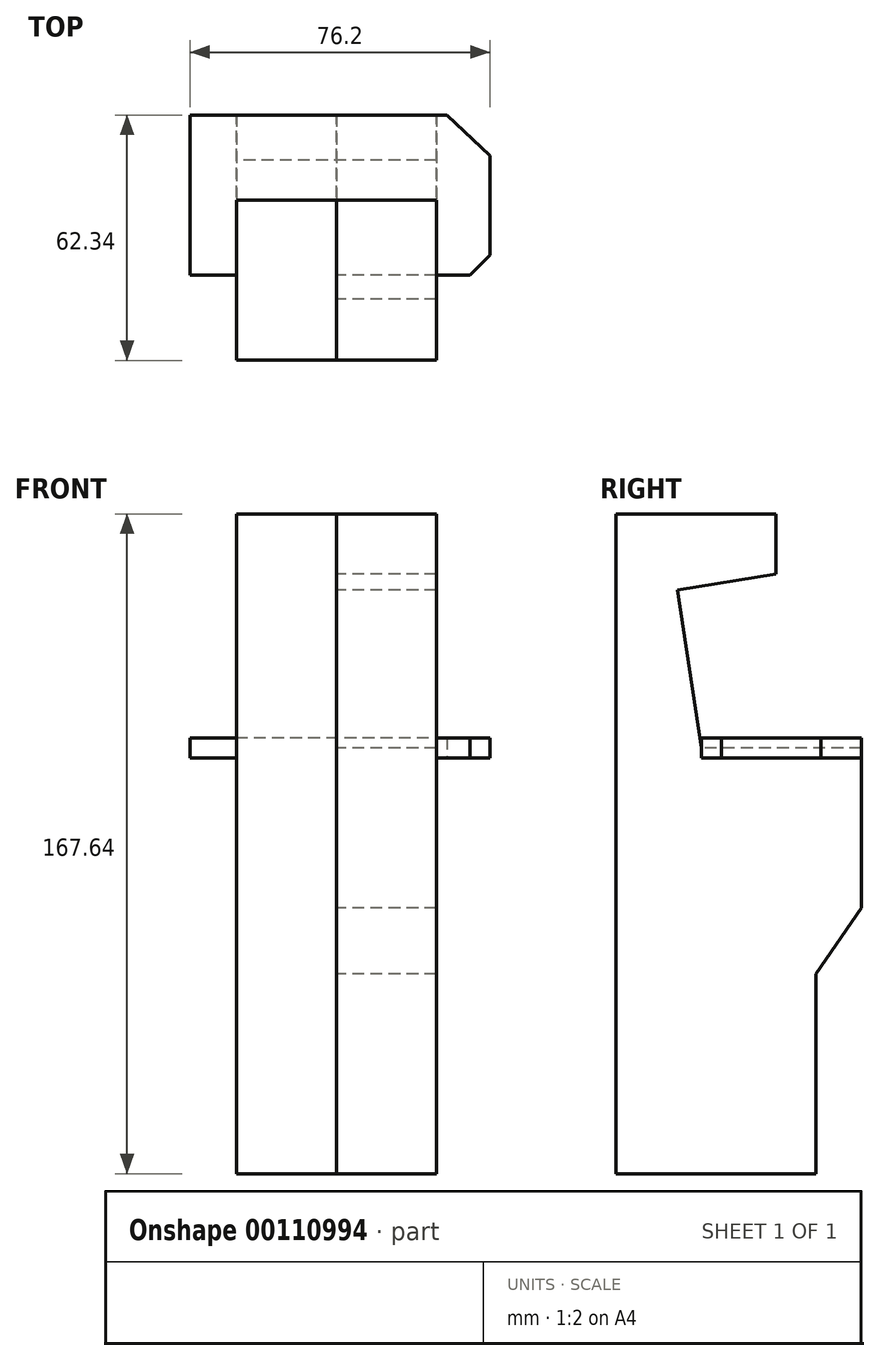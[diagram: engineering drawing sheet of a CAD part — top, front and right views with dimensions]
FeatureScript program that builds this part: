
annotation { "Feature Type Name" : "Feature", "Feature Type Description" : "" }
export const myFeature = defineFeature(function(context is Context, id is Id, definition is map)
    precondition{}
    {
        {
            var Q0;
            Q0=qCreatedBy(makeId("Right.planeOp"),FACE);
            var sketch = newSketch(context, id + "F0", { "sketchPlane" : qUnion([Q0])});
            skLineSegment(sketch, "E0", {"start": v(-55.45, 59.37) * mm, "end": v(-55.45, -108.27) * mm});
            skLineSegment(sketch, "E1", {"start": v(-55.45, 59.37) * mm, "end": v(-14.8, 59.37) * mm});
            skLineSegment(sketch, "E2", {"start": v(-14.8, 59.37) * mm, "end": v(-14.8, 44.13) * mm});
            skLineSegment(sketch, "E3", {"start": v(-55.45, -108.27) * mm, "end": v(-4.65, -108.27) * mm});
            skLineSegment(sketch, "E4", {"start": v(-4.65, -108.27) * mm, "end": v(-4.65, -57.47) * mm});
            skLineSegment(sketch, "E5", {"start": v(-4.65, -57.47) * mm, "end": v(6.9, -40.74) * mm});
            skLineSegment(sketch, "E6", {"start": v(6.9, -40.74) * mm, "end": v(6.9, -0.1) * mm});
            skLineSegment(sketch, "E7", {"start": v(6.9, -0.1) * mm, "end": v(-33.75, -0.1) * mm});
            skLineSegment(sketch, "E8", {"start": v(-14.8, 44.13) * mm, "end": v(-39.88, 40.08) * mm});
            skLineSegment(sketch, "E9", {"start": v(-39.88, 40.08) * mm, "end": v(-33.75, -0.1) * mm});
            skSolve(sketch);
        }
        {
            var Q0;
            Q0 = qSketchRegion(id + "F0", true);
            extrude(context, id + "F1", {"entities" : qUnion([Q0]), "endBound" : BoundingType.SYMMETRIC, "depth" : 50.8 * mm});
        }
        {
            var Q0;
            Q0=makeQuery(id+"F1.opExtrude","SWEPT_FACE",FACE,{"disambiguationData":[OSD([sQuery(id+"F0.wireOp",EDGE,"E7")])]});
            var sketch = newSketch(context, id + "F2", { "sketchPlane" : qUnion([Q0])});
            skLineSegment(sketch, "E10.bottom", {"start": v(38.99, -33.75) * mm, "end": v(-37.21, -33.75) * mm});
            skLineSegment(sketch, "E10.top", {"start": v(28.02, 6.9) * mm, "end": v(-37.21, 6.9) * mm});
            skLineSegment(sketch, "E10.left", {"start": v(38.99, -33.75) * mm, "end": v(38.99, -3.44) * mm});
            skLineSegment(sketch, "E10.right", {"start": v(-37.21, -33.75) * mm, "end": v(-37.21, 6.9) * mm});
            skLineSegment(sketch, "E11", {"start": v(38.99, -3.44) * mm, "end": v(28.02, 6.9) * mm});
            skSolve(sketch);
        }
        {
            var Q0;
            Q0 = qSketchRegion(id + "F2", true);
            extrude(context, id + "F3", {"entities" : qUnion([Q0]), "operationType" : NewBodyOperationType.ADD, "endBound" : BoundingType.SYMMETRIC, "depth" : 5.08 * mm});
        }
        {
            var Q0;
            Q0=makeQuery(id+"F3.opExtrude","SWEPT_EDGE",EDGE,{"disambiguationData":[OSD([sQuery(id+"F2.wireOp",EDGE,"E10.bottom"),sQuery(id+"F2.wireOp",EDGE,"E10.left")])]});
            chamfer(context, id + "F4", {"entities" : qUnion([Q0]), "width" : 5.08 * mm, "tangentPropagation" : true});
        }
        {
            var Q0;
            Q0=makeQuery(id+"F0.imprint","IMPRINT",FACE,{"disambiguationData":[TD([[makeQuery(id+"F0.imprint","IMPRINT",EDGE,{"derivedFrom":sQuery(id+"F0.wireOp",EDGE,"E0")}),1.0]])]});
            extrude(context, id + "F5", {"entities" : qUnion([Q0]), "depth" : 25.4 * mm});
        }
    });
